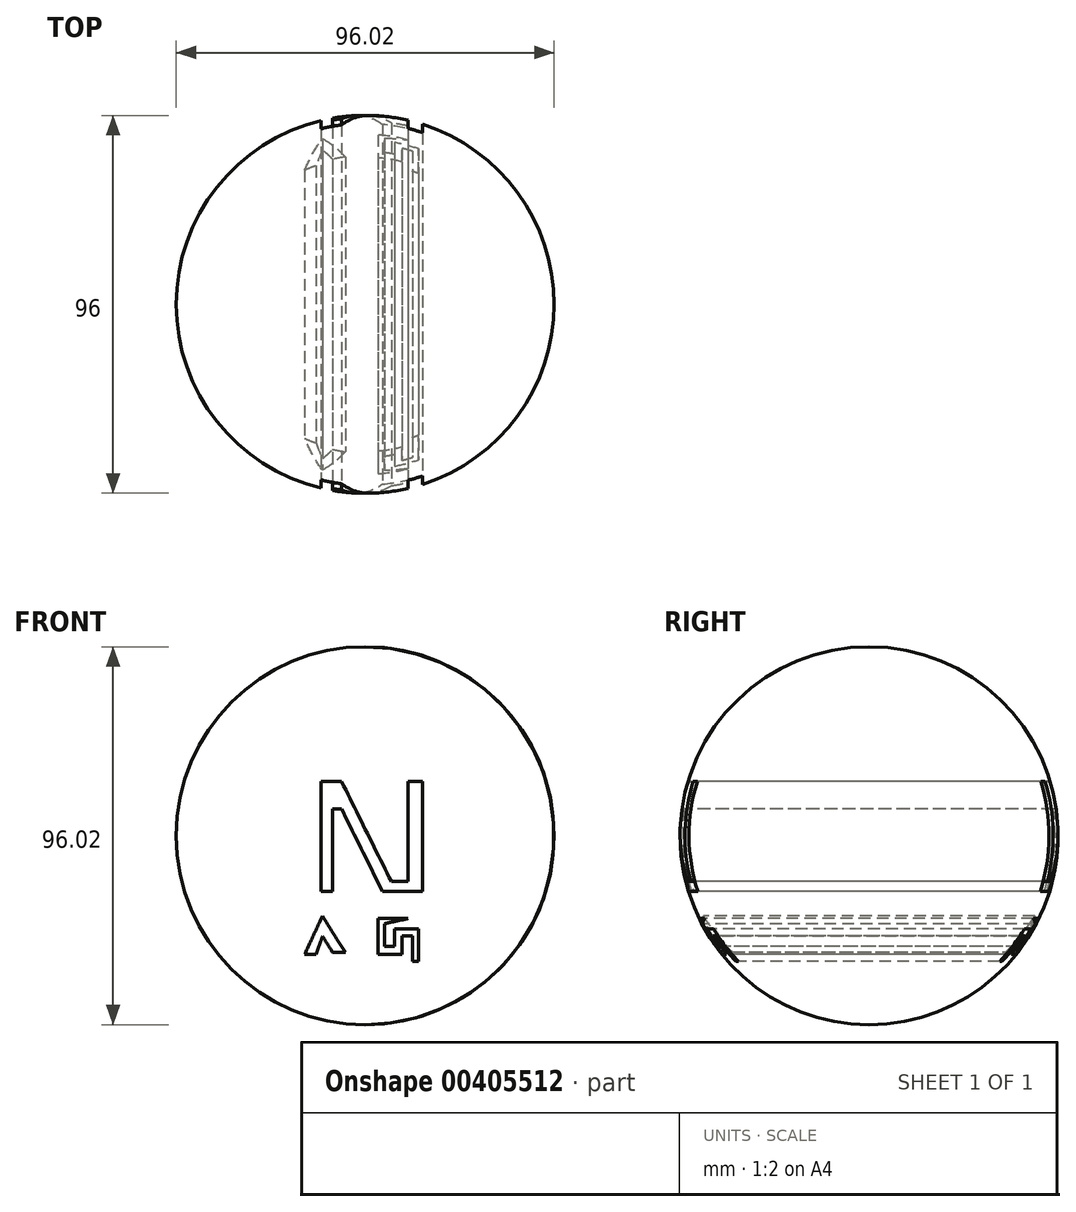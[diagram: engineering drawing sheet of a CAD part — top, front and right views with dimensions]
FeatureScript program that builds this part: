
annotation { "Feature Type Name" : "Feature", "Feature Type Description" : "" }
export const myFeature = defineFeature(function(context is Context, id is Id, definition is map)
    precondition{}
    {
        {
            var Q0;
            Q0=qCreatedBy(makeId("Front.planeOp"),FACE);
            var sketch = newSketch(context, id + "F0", { "sketchPlane" : qUnion([Q0])});
            skLineSegment(sketch, "E0", {"start": v(0, 48) * mm, "end": v(0, -48) * mm});
            skArc(sketch, "E1", {"start": v(0, -48) * mm, "mid": v(48, 0) * mm, "end": v(0, 48) * mm});
            skSolve(sketch);
        }
        {
            var Q0;
            Q0 = qSketchRegion(id + "F0", true);
            var Q1;
            Q1=sQuery(id+"F0.wireOp",EDGE,"E0");
            revolve(context, id + "F1", {"entities" : qUnion([Q0]), "axis" : qUnion([Q1]), "revolveType" : RevolveType.FULL});
        }
        {
            var Q0;
            Q0=qCreatedBy(makeId("Front.planeOp"),FACE);
            var sketch = newSketch(context, id + "F2", { "sketchPlane" : qUnion([Q0])});
            skLineSegment(sketch, "E2", {"start": v(-11.18, -11.66) * mm, "end": v(-11.18, 13.77) * mm});
            skLineSegment(sketch, "E3", {"start": v(-11.18, 13.77) * mm, "end": v(-6, 13.77) * mm});
            skLineSegment(sketch, "E4", {"start": v(-6, 13.77) * mm, "end": v(6.64, -11.66) * mm});
            skLineSegment(sketch, "E5", {"start": v(6.64, -11.66) * mm, "end": v(10.85, -11.66) * mm});
            skLineSegment(sketch, "E6", {"start": v(10.85, -11.66) * mm, "end": v(10.85, 13.77) * mm});
            skLineSegment(sketch, "E7", {"start": v(10.85, 13.77) * mm, "end": v(14.58, 13.77) * mm});
            skLineSegment(sketch, "E8", {"start": v(14.58, 13.77) * mm, "end": v(14.58, -14.1) * mm});
            skLineSegment(sketch, "E9", {"start": v(14.58, -14.1) * mm, "end": v(4.37, -14.1) * mm});
            skLineSegment(sketch, "E10", {"start": v(4.37, -14.1) * mm, "end": v(-6, 6.77) * mm});
            skLineSegment(sketch, "E11", {"start": v(-6, 6.77) * mm, "end": v(-8.26, 6.77) * mm});
            skLineSegment(sketch, "E12", {"start": v(-8.26, 6.77) * mm, "end": v(-8.26, -14.1) * mm});
            skLineSegment(sketch, "E13", {"start": v(-8.26, -14.1) * mm, "end": v(-11.18, -14.1) * mm});
            skLineSegment(sketch, "E14", {"start": v(-11.18, -14.1) * mm, "end": v(-11.18, -11.66) * mm});
            skLineSegment(sketch, "E15", {"start": v(-12.47, -30.13) * mm, "end": v(-15.39, -30.13) * mm});
            skLineSegment(sketch, "E16", {"start": v(-15.39, -30.13) * mm, "end": v(-10.85, -20.4) * mm});
            skLineSegment(sketch, "E17", {"start": v(-10.85, -20.4) * mm, "end": v(-5.02, -29.64) * mm});
            skLineSegment(sketch, "E18", {"start": v(-5.02, -29.64) * mm, "end": v(-8.26, -29.64) * mm});
            skLineSegment(sketch, "E19", {"start": v(-8.26, -29.64) * mm, "end": v(-10.85, -25.54) * mm});
            skLineSegment(sketch, "E20", {"start": v(-10.85, -25.54) * mm, "end": v(-12.47, -30.13) * mm});
            skLineSegment(sketch, "E21", {"start": v(10.85, -21.06) * mm, "end": v(3.24, -21.06) * mm});
            skLineSegment(sketch, "E22", {"start": v(3.24, -21.06) * mm, "end": v(3.24, -30.13) * mm});
            skLineSegment(sketch, "E23", {"start": v(3.24, -30.13) * mm, "end": v(9.4, -30.13) * mm});
            skLineSegment(sketch, "E24", {"start": v(9.4, -30.13) * mm, "end": v(9.4, -25.43) * mm});
            skLineSegment(sketch, "E25", {"start": v(9.4, -25.43) * mm, "end": v(11.99, -25.43) * mm});
            skLineSegment(sketch, "E26", {"start": v(11.99, -25.43) * mm, "end": v(11.99, -31.9) * mm});
            skLineSegment(sketch, "E27", {"start": v(11.99, -31.9) * mm, "end": v(13.6, -31.9) * mm});
            skLineSegment(sketch, "E28", {"start": v(13.6, -31.9) * mm, "end": v(13.6, -23.65) * mm});
            skLineSegment(sketch, "E29", {"start": v(13.6, -23.65) * mm, "end": v(9.4, -23.65) * mm});
            skLineSegment(sketch, "E30", {"start": v(9.4, -23.65) * mm, "end": v(7.45, -23.65) * mm});
            skLineSegment(sketch, "E31", {"start": v(7.45, -23.65) * mm, "end": v(7.45, -28.18) * mm});
            skLineSegment(sketch, "E32", {"start": v(7.45, -28.18) * mm, "end": v(4.86, -28.18) * mm});
            skLineSegment(sketch, "E33", {"start": v(4.86, -28.18) * mm, "end": v(4.86, -22.35) * mm});
            skLineSegment(sketch, "E34", {"start": v(4.86, -22.35) * mm, "end": v(10.85, -21.06) * mm});
            skSolve(sketch);
        }
        {
            var Q0;
            Q0 = qSketchRegion(id + "F2", true);
            extrude(context, id + "F3", {"entities" : qUnion([Q0]), "operationType" : NewBodyOperationType.REMOVE, "endBound" : BoundingType.SYMMETRIC, "oppositeDirection" : true, "depth" : 127 * mm});
        }
    });
